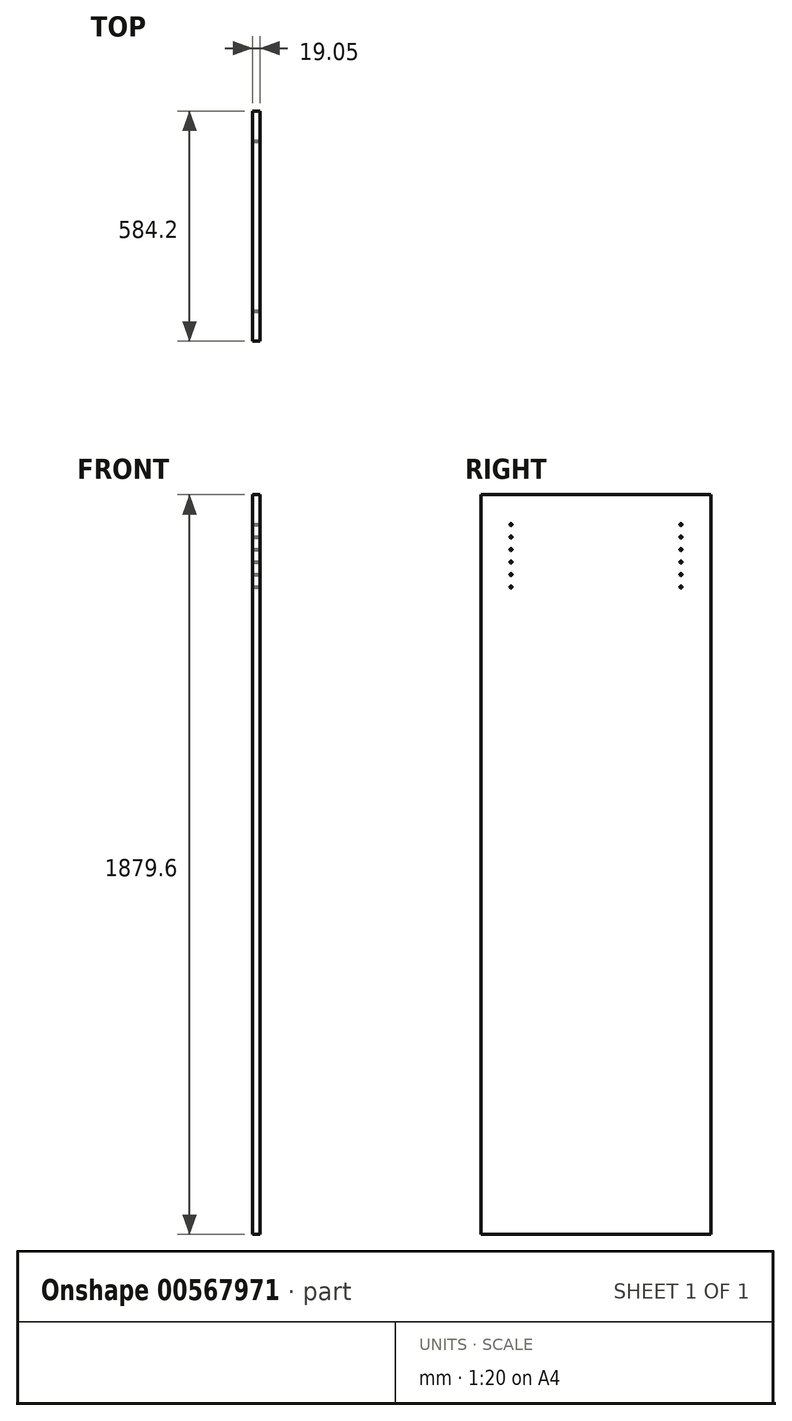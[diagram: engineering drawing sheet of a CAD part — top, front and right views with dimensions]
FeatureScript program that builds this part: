
annotation { "Feature Type Name" : "Feature", "Feature Type Description" : "" }
export const myFeature = defineFeature(function(context is Context, id is Id, definition is map)
    precondition{}
    {
        {
            var Q0;
            Q0=qCreatedBy(makeId("Right.planeOp"),FACE);
            var sketch = newSketch(context, id + "F0", { "sketchPlane" : qUnion([Q0])});
            skLineSegment(sketch, "E0.bottom", {"start": v(292.1, 939.8) * mm, "end": v(-292.1, 939.8) * mm});
            skLineSegment(sketch, "E0.top", {"start": v(292.1, -939.8) * mm, "end": v(-292.1, -939.8) * mm});
            skLineSegment(sketch, "E0.left", {"start": v(292.1, 939.8) * mm, "end": v(292.1, -939.8) * mm});
            skLineSegment(sketch, "E0.right", {"start": v(-292.1, 939.8) * mm, "end": v(-292.1, -939.8) * mm});
            skPoint(sketch, "E0.middle", {"position": v(0, 0) * mm});
            skSolve(sketch);
        }
        {
            var Q0;
            Q0=makeQuery(id+"F0.imprint","IMPRINT",FACE,{"disambiguationData":[TD([[makeQuery(id+"F0.imprint","IMPRINT",EDGE,{"derivedFrom":sQuery(id+"F0.wireOp",EDGE,"E0.bottom")}),1.0]])]});
            extrude(context, id + "F1", {"entities" : qUnion([Q0]), "depth" : 19.05 * mm, "offsetDistance" : 25.4 * mm});
        }
        {
            var Q0;
            Q0=makeQuery(id+"F1.opExtrude","CAP_FACE",FACE,{"disambiguationData":[OSD([sQuery(id+"F0.wireOp",EDGE,"E0.bottom"),sQuery(id+"F0.wireOp",EDGE,"E0.top"),sQuery(id+"F0.wireOp",EDGE,"E0.left"),sQuery(id+"F0.wireOp",EDGE,"E0.right")])],"isStart":false});
            var sketch = newSketch(context, id + "F2", { "sketchPlane" : qUnion([Q0])});
            skLineSegment(sketch, "E1", {"start": v(-292.1, 939.8) * mm, "end": v(-292.1, 863.6) * mm});
            skLineSegment(sketch, "E2", {"start": v(-292.1, 863.6) * mm, "end": v(292.1, 863.6) * mm});
            skLineSegment(sketch, "E3", {"start": v(292.1, 863.6) * mm, "end": v(292.1, 831.85) * mm});
            skLineSegment(sketch, "E4", {"start": v(292.1, 831.85) * mm, "end": v(-292.1, 831.85) * mm});
            skLineSegment(sketch, "E5", {"start": v(-292.1, 831.85) * mm, "end": v(-292.1, 800.1) * mm});
            skLineSegment(sketch, "E6", {"start": v(-292.1, 800.1) * mm, "end": v(292.1, 800.1) * mm});
            skLineSegment(sketch, "E7", {"start": v(292.1, 800.1) * mm, "end": v(292.1, 768.35) * mm});
            skLineSegment(sketch, "E8", {"start": v(292.1, 768.35) * mm, "end": v(-292.1, 768.35) * mm});
            skLineSegment(sketch, "E9", {"start": v(-292.1, 768.35) * mm, "end": v(-292.1, 736.6) * mm});
            skLineSegment(sketch, "E10", {"start": v(-292.1, 736.6) * mm, "end": v(292.1, 736.6) * mm});
            skLineSegment(sketch, "E11", {"start": v(-292.1, 863.6) * mm, "end": v(-215.9, 863.6) * mm});
            skLineSegment(sketch, "E12", {"start": v(-215.9, 863.6) * mm, "end": v(-215.9, 736.6) * mm});
            skLineSegment(sketch, "E13", {"start": v(292.1, 863.6) * mm, "end": v(215.9, 863.6) * mm});
            skLineSegment(sketch, "E14", {"start": v(215.9, 863.6) * mm, "end": v(215.9, 736.6) * mm});
            skPoint(sketch, "E15", {"position": v(-215.9, 863.6) * mm});
            skPoint(sketch, "E16", {"position": v(-215.9, 800.1) * mm});
            skPoint(sketch, "E17", {"position": v(-215.9, 736.6) * mm});
            skPoint(sketch, "E18", {"position": v(215.9, 863.6) * mm});
            skPoint(sketch, "E19", {"position": v(215.9, 800.1) * mm});
            skPoint(sketch, "E20", {"position": v(215.9, 736.6) * mm});
            skPoint(sketch, "E21", {"position": v(-215.9, 831.85) * mm});
            skPoint(sketch, "E22", {"position": v(-215.9, 768.35) * mm});
            skPoint(sketch, "E23", {"position": v(215.9, 831.85) * mm});
            skPoint(sketch, "E24", {"position": v(215.9, 768.35) * mm});
            skLineSegment(sketch, "E25", {"start": v(-215.9, 736.6) * mm, "end": v(-215.9, 704.85) * mm});
            skLineSegment(sketch, "E26", {"start": v(215.9, 736.6) * mm, "end": v(215.9, 704.85) * mm});
            skPoint(sketch, "E27", {"position": v(-215.9, 704.85) * mm});
            skPoint(sketch, "E28", {"position": v(215.9, 704.85) * mm});
            skSolve(sketch);
        }
        {
            var Q0;
            Q0=sQuery(id+"F2.wireOp",VERTEX,"E15");
            var Q1;
            Q1=sQuery(id+"F2.wireOp",VERTEX,"E21");
            var Q2;
            Q2=sQuery(id+"F2.wireOp",VERTEX,"E16");
            var Q3;
            Q3=sQuery(id+"F2.wireOp",VERTEX,"E22");
            var Q4;
            Q4=sQuery(id+"F2.wireOp",VERTEX,"E17");
            var Q5;
            Q5=sQuery(id+"F2.wireOp",VERTEX,"E18");
            var Q6;
            Q6=sQuery(id+"F2.wireOp",VERTEX,"E23");
            var Q7;
            Q7=sQuery(id+"F2.wireOp",VERTEX,"E19");
            var Q8;
            Q8=sQuery(id+"F2.wireOp",VERTEX,"E24");
            var Q9;
            Q9=sQuery(id+"F2.wireOp",VERTEX,"E20");
            var Q10;
            Q10=sQuery(id+"F2.wireOp",VERTEX,"f382819e-2962-4759-8f64-b7ce76b9eab9");
            var Q11;
            Q11=sQuery(id+"F2.wireOp",VERTEX,"758ac672-c17d-402f-be1e-20a9f19c910d");
            var Q12;
            Q12=sQuery(id+"F2.wireOp",VERTEX,"fdadfb9e-047b-40be-af7f-0b44bd3a180c");
            var Q13;
            Q13=sQuery(id+"F2.wireOp",VERTEX,"bc5b2b74-7b9a-4213-9ffc-5d99cdb1b0f4");
            var Q14;
            Q14=sQuery(id+"F2.wireOp",VERTEX,"7411fb6c-7a7b-458d-890c-a4140a39a52e");
            var Q15;
            Q15=sQuery(id+"F2.wireOp",VERTEX,"bcfb4890-0eb3-4105-a0bc-92a74f4c52fa");
            var Q16;
            Q16=sQuery(id+"F2.wireOp",VERTEX,"a4e1c321-4b63-49a8-b259-f64a3b119249");
            var Q17;
            Q17=sQuery(id+"F2.wireOp",VERTEX,"6d0e744e-bf45-4f34-8df6-d49a30ab025f");
            var Q18;
            Q18=sQuery(id+"F2.wireOp",VERTEX,"921f37f3-7255-42e2-8430-325583f77f6a");
            var Q19;
            Q19=sQuery(id+"F2.wireOp",VERTEX,"3b08a2c2-9617-479f-b4ba-e89e814900d1");
            var Q20;
            Q20=sQuery(id+"F2.wireOp",VERTEX,"E27");
            var Q21;
            Q21=sQuery(id+"F2.wireOp",VERTEX,"E28");
            var Q22;
            Q22=sQuery(id+"F2.wireOp",VERTEX,"a4e313b6-6f36-4783-9699-c7d12b9612c9");
            var Q23;
            Q23=sQuery(id+"F2.wireOp",VERTEX,"012cc85f-7bdb-495c-a166-fe9a72951d4d");
            var Q24;
            Q24=makeQuery(id+"F1.opExtrude","SWEPT_BODY",BODY,{"disambiguationData":[OSD([sQuery(id+"F0.wireOp",EDGE,"E0.bottom"),sQuery(id+"F0.wireOp",EDGE,"E0.top"),sQuery(id+"F0.wireOp",EDGE,"E0.left"),sQuery(id+"F0.wireOp",EDGE,"E0.right")])]});
            hole(context, id + "F3", {"style" : HoleStyle.SIMPLE, "endStyle" : HoleEndStyle.BLIND, "holeDiameter" : 5 * mm, "holeDepth" : 14.22 * mm, "isTappedThrough" : true, "tappedDepth" : 12.7 * mm, "tapClearance" : 3, "startFromSketch" : true, "locations" : qUnion([Q0, Q1, Q2, Q3, Q4, Q5, Q6, Q7, Q8, Q9, Q10, Q11, Q12, Q13, Q14, Q15, Q16, Q17, Q18, Q19, Q20, Q21, Q22, Q23]), "scope" : qUnion([Q24])});
        }
    });
